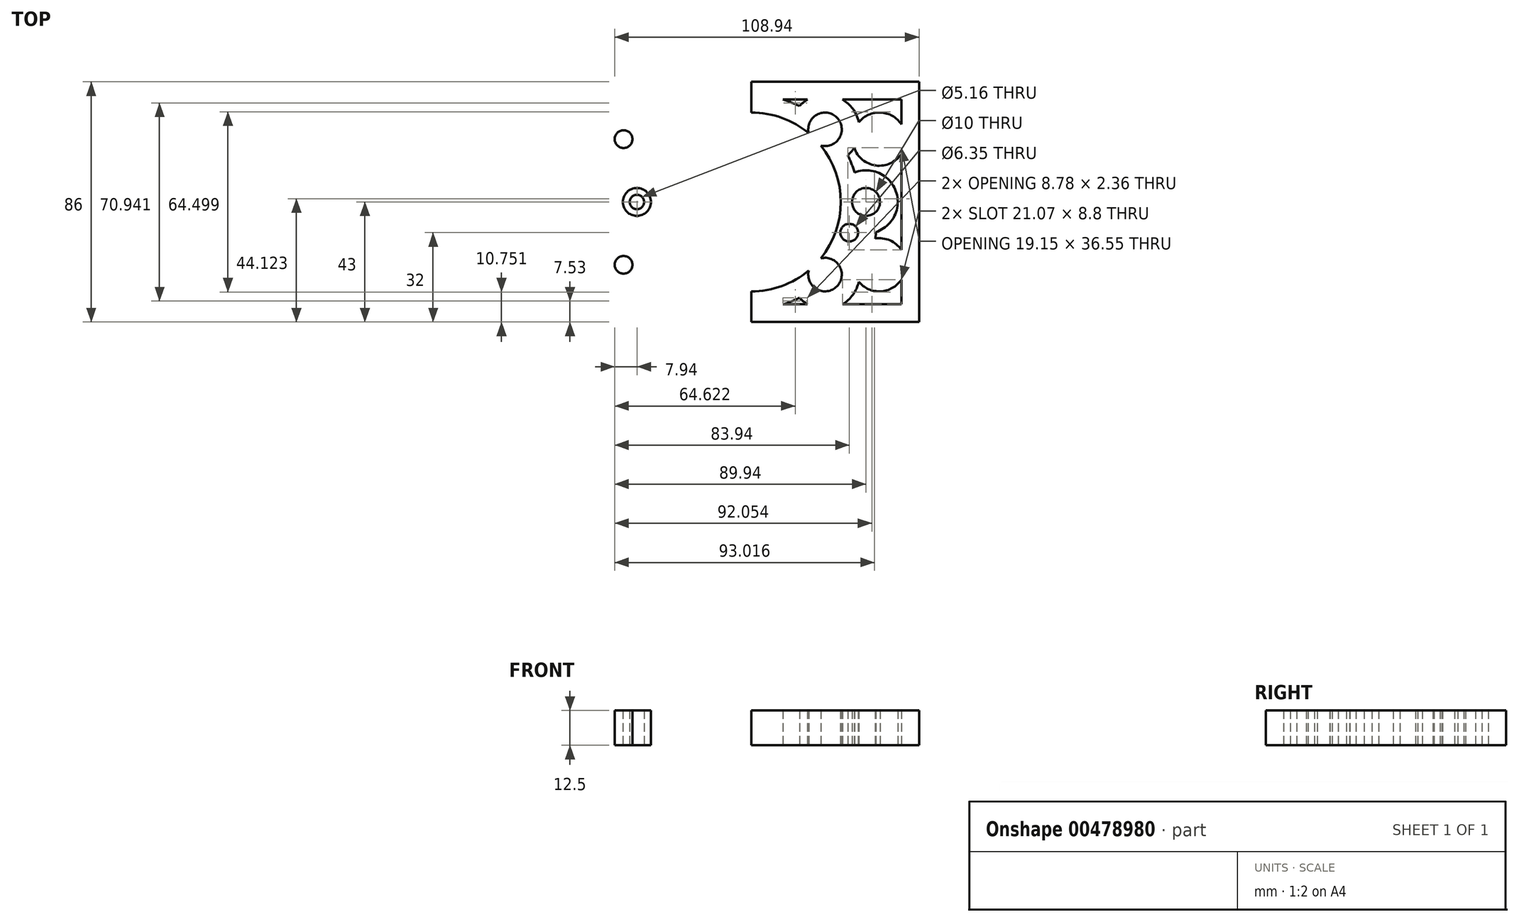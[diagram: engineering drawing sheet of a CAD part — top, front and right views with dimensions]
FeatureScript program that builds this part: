
annotation { "Feature Type Name" : "Feature", "Feature Type Description" : "" }
export const myFeature = defineFeature(function(context is Context, id is Id, definition is map)
    precondition{}
    {
        {
            var Q0;
            Q0=qCreatedBy(makeId("Top.planeOp"),FACE);
            var sketch = newSketch(context, id + "F0", { "sketchPlane" : qUnion([Q0])});
            skLineSegment(sketch, "E0", {"start": v(0, 60) * mm, "end": v(0, -60) * mm});
            skLineSegment(sketch, "E1", {"start": v(-70, 0) * mm, "end": v(70, 0) * mm});
            skLineSegment(sketch, "E2", {"start": v(-60, 43) * mm, "end": v(60, 43) * mm});
            skLineSegment(sketch, "E3", {"start": v(-60, -43) * mm, "end": v(60, -43) * mm});
            skCircle(sketch, "E4", {"center": v(-45.77, 22.5) * mm, "radius": 3.17 * mm});
            skCircle(sketch, "E5", {"center": v(-45.77, -22.5) * mm, "radius": 3.17 * mm});
            skCircle(sketch, "E6", {"center": v(45.77, -22.5) * mm, "radius": 3.17 * mm});
            skCircle(sketch, "E7", {"center": v(45.77, 22.5) * mm, "radius": 3.17 * mm});
            skCircle(sketch, "E8", {"center": v(-41, 0) * mm, "radius": 2.58 * mm});
            skCircle(sketch, "E9", {"center": v(41, 0) * mm, "radius": 2.58 * mm});
            skCircle(sketch, "E10", {"center": v(-41, 0) * mm, "radius": 5 * mm});
            skCircle(sketch, "E11", {"center": v(41, 0) * mm, "radius": 5 * mm});
            skLineSegment(sketch, "E12", {"start": v(60, 43) * mm, "end": v(60, -43) * mm});
            skLineSegment(sketch, "E13", {"start": v(-60, 43) * mm, "end": v(-60, -43) * mm});
            skArc(sketch, "E14", {"start": v(-24.83, 20.2) * mm, "mid": v(-32, 0) * mm, "end": v(-24.83, -20.2) * mm});
            skArc(sketch, "E15", {"start": v(-20.5, 24.57) * mm, "mid": v(-30.6, 30.22) * mm, "end": v(-24.83, 20.2) * mm});
            skArc(sketch, "E16", {"start": v(24.83, 20.2) * mm, "mid": v(30.6, 30.22) * mm, "end": v(20.5, 24.57) * mm});
            skArc(sketch, "E17", {"start": v(20.5, -24.57) * mm, "mid": v(30.6, -30.22) * mm, "end": v(24.83, -20.2) * mm});
            skArc(sketch, "E18", {"start": v(-24.83, -20.2) * mm, "mid": v(-30.6, -30.22) * mm, "end": v(-20.5, -24.57) * mm});
            skArc(sketch, "E19", {"start": v(20.5, 24.57) * mm, "mid": v(0, 32) * mm, "end": v(-20.5, 24.57) * mm});
            skArc(sketch, "E20", {"start": v(-20.5, -24.57) * mm, "mid": v(0, -32) * mm, "end": v(20.5, -24.57) * mm});
            skArc(sketch, "E21", {"start": v(24.83, -20.2) * mm, "mid": v(32, 0) * mm, "end": v(24.83, 20.2) * mm});
            skCircle(sketch, "E22", {"center": v(35, -11) * mm, "radius": 3.17 * mm});
            skArc(sketch, "E23", {"start": v(-53.65, 17.15) * mm, "mid": v(-44.51, 13.06) * mm, "end": v(-36.76, 19.4) * mm});
            skArc(sketch, "E24", {"start": v(-36.76, -19.4) * mm, "mid": v(-44.51, -13.06) * mm, "end": v(-53.65, -17.15) * mm});
            skArc(sketch, "E25", {"start": v(-36.86, 10.57) * mm, "mid": v(-52.35, 0) * mm, "end": v(-36.86, -10.57) * mm});
            skLineSegment(sketch, "E26", {"start": v(-53.65, 36.65) * mm, "end": v(-53.65, 27.85) * mm});
            skLineSegment(sketch, "E27", {"start": v(-53.65, -36.65) * mm, "end": v(-32.58, -36.65) * mm});
            skLineSegment(sketch, "E28", {"start": v(53.65, 36.65) * mm, "end": v(53.65, 27.85) * mm});
            skArc(sketch, "E29", {"start": v(-34.5, -16.74) * mm, "mid": v(-35.73, -18) * mm, "end": v(-36.76, -19.4) * mm});
            skArc(sketch, "E30", {"start": v(-17.17, -34.3) * mm, "mid": v(-14.28, -35.6) * mm, "end": v(-11.3, -36.65) * mm});
            skArc(sketch, "E31", {"start": v(17.17, 34.3) * mm, "mid": v(14.28, 35.6) * mm, "end": v(11.3, 36.65) * mm});
            skArc(sketch, "E32", {"start": v(36.86, 10.57) * mm, "mid": v(35.82, 13.7) * mm, "end": v(34.5, 16.74) * mm});
            skArc(sketch, "E33", {"start": v(-34.5, 16.74) * mm, "mid": v(-35.82, 13.7) * mm, "end": v(-36.86, 10.57) * mm});
            skArc(sketch, "E34", {"start": v(53.65, 27.85) * mm, "mid": v(46.2, 32.02) * mm, "end": v(38.4, 28.55) * mm});
            skArc(sketch, "E35", {"start": v(38.4, -28.55) * mm, "mid": v(46.2, -32.02) * mm, "end": v(53.65, -27.85) * mm});
            skArc(sketch, "E36", {"start": v(44.52, -10.79) * mm, "mid": v(51.68, 3.83) * mm, "end": v(36.86, 10.57) * mm});
            skArc(sketch, "E37", {"start": v(44.3, -13.09) * mm, "mid": v(44.48, -11.95) * mm, "end": v(44.52, -10.79) * mm});
            skArc(sketch, "E38", {"start": v(17.17, -34.3) * mm, "mid": v(18.53, -35.58) * mm, "end": v(20.07, -36.65) * mm});
            skArc(sketch, "E39", {"start": v(-17.17, 34.3) * mm, "mid": v(-18.53, 35.58) * mm, "end": v(-20.07, 36.65) * mm});
            skLineSegment(sketch, "E40", {"start": v(-53.65, 36.65) * mm, "end": v(-32.58, 36.65) * mm});
            skLineSegment(sketch, "E41", {"start": v(-20.07, -36.65) * mm, "end": v(-11.3, -36.65) * mm});
            skArc(sketch, "E42", {"start": v(-38.4, -28.55) * mm, "mid": v(-36.35, -33.21) * mm, "end": v(-32.58, -36.65) * mm});
            skArc(sketch, "E43", {"start": v(-20.07, -36.65) * mm, "mid": v(-18.53, -35.58) * mm, "end": v(-17.17, -34.3) * mm});
            skArc(sketch, "E44", {"start": v(32.58, -36.65) * mm, "mid": v(36.35, -33.21) * mm, "end": v(38.4, -28.55) * mm});
            skArc(sketch, "E45", {"start": v(11.3, -36.65) * mm, "mid": v(14.28, -35.6) * mm, "end": v(17.17, -34.3) * mm});
            skLineSegment(sketch, "E46", {"start": v(11.3, -36.65) * mm, "end": v(20.07, -36.65) * mm});
            skLineSegment(sketch, "E47", {"start": v(-53.65, -27.85) * mm, "end": v(-53.65, -36.65) * mm});
            skArc(sketch, "E48", {"start": v(-53.65, -27.85) * mm, "mid": v(-46.2, -32.02) * mm, "end": v(-38.4, -28.55) * mm});
            skLineSegment(sketch, "E49", {"start": v(32.58, -36.65) * mm, "end": v(53.65, -36.65) * mm});
            skLineSegment(sketch, "E50", {"start": v(53.65, -27.85) * mm, "end": v(53.65, -36.65) * mm});
            skArc(sketch, "E51", {"start": v(53.65, -17.15) * mm, "mid": v(49.56, -13.76) * mm, "end": v(44.3, -13.09) * mm});
            skLineSegment(sketch, "E52", {"start": v(53.65, 17.15) * mm, "end": v(53.65, -17.15) * mm});
            skLineSegment(sketch, "E53", {"start": v(-53.65, 17.15) * mm, "end": v(-53.65, -17.15) * mm});
            skArc(sketch, "E54", {"start": v(-36.86, -10.57) * mm, "mid": v(-35.82, -13.7) * mm, "end": v(-34.5, -16.74) * mm});
            skArc(sketch, "E55", {"start": v(-36.76, 19.4) * mm, "mid": v(-35.73, 18) * mm, "end": v(-34.5, 16.74) * mm});
            skArc(sketch, "E56", {"start": v(-32.58, 36.65) * mm, "mid": v(-36.35, 33.21) * mm, "end": v(-38.4, 28.55) * mm});
            skArc(sketch, "E57", {"start": v(20.07, 36.65) * mm, "mid": v(18.53, 35.58) * mm, "end": v(17.17, 34.3) * mm});
            skLineSegment(sketch, "E58", {"start": v(11.3, 36.65) * mm, "end": v(20.07, 36.65) * mm});
            skLineSegment(sketch, "E59", {"start": v(-20.07, 36.65) * mm, "end": v(-11.3, 36.65) * mm});
            skLineSegment(sketch, "E60", {"start": v(32.58, 36.65) * mm, "end": v(53.65, 36.65) * mm});
            skArc(sketch, "E61", {"start": v(-38.4, 28.55) * mm, "mid": v(-46.2, 32.02) * mm, "end": v(-53.65, 27.85) * mm});
            skArc(sketch, "E62", {"start": v(38.4, 28.55) * mm, "mid": v(36.35, 33.21) * mm, "end": v(32.58, 36.65) * mm});
            skArc(sketch, "E63", {"start": v(-11.3, 36.65) * mm, "mid": v(-14.28, 35.6) * mm, "end": v(-17.17, 34.3) * mm});
            skArc(sketch, "E64", {"start": v(34.5, 16.74) * mm, "mid": v(35.73, 18) * mm, "end": v(36.76, 19.4) * mm});
            skArc(sketch, "E65", {"start": v(36.76, 19.4) * mm, "mid": v(44.51, 13.06) * mm, "end": v(53.65, 17.15) * mm});
            skSolve(sketch);
        }
        {
            var Q0;
            Q0=makeQuery(id+"F0.imprint","IMPRINT",FACE,{"disambiguationData":[TD([[makeQuery(id+"F0.imprint","IMPRINT",EDGE,{"derivedFrom":sQuery(id+"F0.wireOp",EDGE,"E4")}),1.0]])]});
            var Q1;
            Q1=makeQuery(id+"F0.imprint","IMPRINT",FACE,{"disambiguationData":[TD([[makeQuery(id+"F0.imprint","IMPRINT",EDGE,{"derivedFrom":sQuery(id+"F0.wireOp",EDGE,"E5")}),1.0]])]});
            var Q2;
            Q2=makeQuery(id+"F0.imprint","IMPRINT",FACE,{"disambiguationData":[TD([[makeQuery(id+"F0.imprint","IMPRINT",EDGE,{"derivedFrom":sQuery(id+"F0.wireOp",EDGE,"E6")}),1.0]])]});
            var Q3;
            Q3=makeQuery(id+"F0.imprint","IMPRINT",FACE,{"disambiguationData":[TD([[makeQuery(id+"F0.imprint","IMPRINT",EDGE,{"derivedFrom":sQuery(id+"F0.wireOp",EDGE,"E7")}),1.0]])]});
            var Q4;
            {var subQ0=sQuery(id+"F0.wireOp",EDGE,"E10");var subQ1=sQuery(id+"F0.wireOp",EDGE,"E1");var subQ2=makeQuery(id+"F0.imprint","INTERSECT",VERTEX,{"disambiguationData":[OD(0.0)],"derivedFrom":[subQ1,subQ0]});Q4=makeQuery(id+"F0.imprint","IMPRINT",FACE,{"disambiguationData":[TD([[makeQuery(id+"F0.imprint","IMPRINT",EDGE,{"disambiguationData":[TD([[subQ2,-1.0]])],"derivedFrom":subQ1}),1.0]])]});}
            var Q5;
            {var subQ0=sQuery(id+"F0.wireOp",EDGE,"E10");var subQ1=sQuery(id+"F0.wireOp",EDGE,"E1");var subQ2=makeQuery(id+"F0.imprint","INTERSECT",VERTEX,{"disambiguationData":[OD(0.0)],"derivedFrom":[subQ1,subQ0]});Q5=makeQuery(id+"F0.imprint","IMPRINT",FACE,{"disambiguationData":[TD([[makeQuery(id+"F0.imprint","IMPRINT",EDGE,{"disambiguationData":[TD([[subQ2,-1.0]])],"derivedFrom":subQ1}),-1.0]])]});}
            var Q6;
            {var subQ0=sQuery(id+"F0.wireOp",EDGE,"E11");var subQ1=sQuery(id+"F0.wireOp",EDGE,"E1");var subQ2=makeQuery(id+"F0.imprint","INTERSECT",VERTEX,{"disambiguationData":[OD(0.0)],"derivedFrom":[subQ1,subQ0]});Q6=makeQuery(id+"F0.imprint","IMPRINT",FACE,{"disambiguationData":[TD([[makeQuery(id+"F0.imprint","IMPRINT",EDGE,{"disambiguationData":[TD([[subQ2,-1.0]])],"derivedFrom":subQ1}),1.0]])]});}
            var Q7;
            {var subQ0=sQuery(id+"F0.wireOp",EDGE,"E11");var subQ1=sQuery(id+"F0.wireOp",EDGE,"E1");var subQ2=makeQuery(id+"F0.imprint","INTERSECT",VERTEX,{"disambiguationData":[OD(0.0)],"derivedFrom":[subQ1,subQ0]});Q7=makeQuery(id+"F0.imprint","IMPRINT",FACE,{"disambiguationData":[TD([[makeQuery(id+"F0.imprint","IMPRINT",EDGE,{"disambiguationData":[TD([[subQ2,-1.0]])],"derivedFrom":subQ1}),-1.0]])]});}
            extrude(context, id + "F1", {"entities" : qUnion([Q0, Q1, Q2, Q3, Q4, Q5, Q6, Q7]), "depth" : 12.5 * mm});
        }
    });
